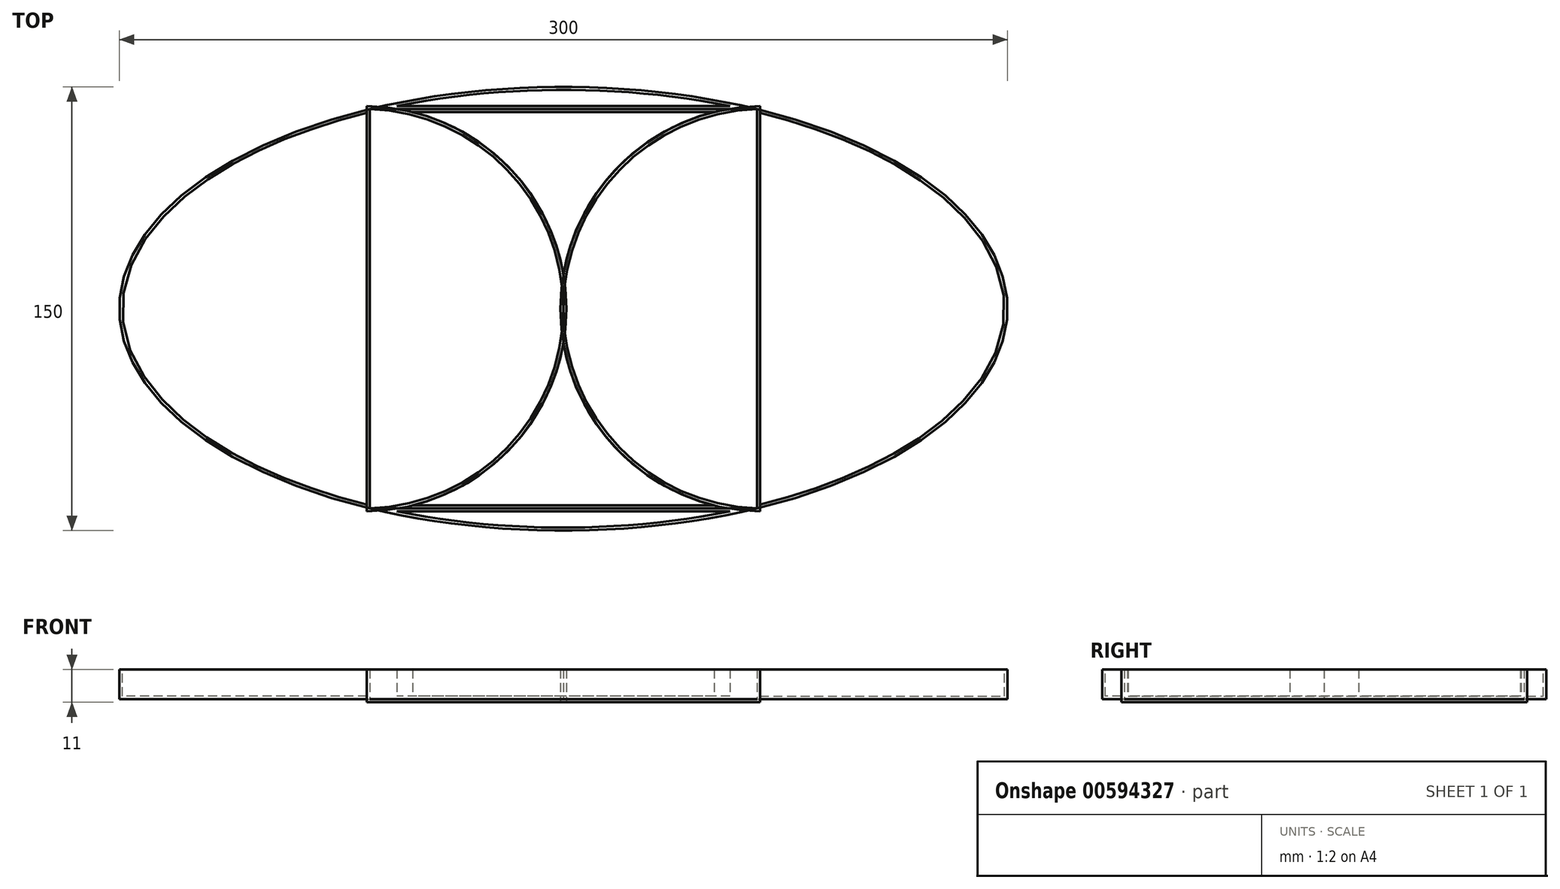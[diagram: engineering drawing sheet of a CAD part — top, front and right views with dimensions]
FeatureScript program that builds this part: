
annotation { "Feature Type Name" : "Feature", "Feature Type Description" : "" }
export const myFeature = defineFeature(function(context is Context, id is Id, definition is map)
    precondition{}
    {
        {
            var Q0;
            Q0=qCreatedBy(makeId("Top.planeOp"),FACE);
            var sketch = newSketch(context, id + "F0", { "sketchPlane" : qUnion([Q0])});
            skEllipse(sketch, "E0", {"center": v(0, 0) * mm, "majorRadius": 150 * mm, "minorRadius": 75 * mm, "majorAxis": v(1, 0)});
            skLineSegment(sketch, "E1.bottom", {"start": v(65.38, 67.5) * mm, "end": v(-65.38, 67.5) * mm});
            skLineSegment(sketch, "E1.top", {"start": v(65.38, -67.5) * mm, "end": v(-65.38, -67.5) * mm});
            skLineSegment(sketch, "E1.left", {"start": v(65.38, 67.5) * mm, "end": v(65.38, -67.5) * mm});
            skLineSegment(sketch, "E1.right", {"start": v(-65.38, 67.5) * mm, "end": v(-65.38, -67.5) * mm});
            skArc(sketch, "E2", {"start": v(-65.38, -67.5) * mm, "mid": v(0, 0) * mm, "end": v(-65.38, 67.5) * mm});
            skArc(sketch, "E3", {"start": v(65.38, 67.5) * mm, "mid": v(0, 0) * mm, "end": v(65.38, -67.5) * mm});
            skSolve(sketch);
        }
        {
            var Q0;
            {var subQ1=sQuery(id+"F0.wireOp",EDGE,"E1.right");Q0=makeQuery(id+"F0.imprint","IMPRINT",FACE,{"disambiguationData":[TD([[makeQuery(id+"F0.imprint","IMPRINT",EDGE,{"derivedFrom":subQ1}),-1.0]])]});}
            var Q1;
            {var subQ0=sQuery(id+"F0.wireOp",EDGE,"E1.bottom");Q1=makeQuery(id+"F0.imprint","IMPRINT",FACE,{"disambiguationData":[TD([[makeQuery(id+"F0.imprint","IMPRINT",EDGE,{"derivedFrom":subQ0}),-1.0]])]});}
            var Q2;
            {var subQ1=sQuery(id+"F0.wireOp",EDGE,"E1.left");Q2=makeQuery(id+"F0.imprint","IMPRINT",FACE,{"disambiguationData":[TD([[makeQuery(id+"F0.imprint","IMPRINT",EDGE,{"derivedFrom":subQ1}),1.0]])]});}
            var Q3;
            {var subQ0=sQuery(id+"F0.wireOp",EDGE,"E1.top");Q3=makeQuery(id+"F0.imprint","IMPRINT",FACE,{"disambiguationData":[TD([[makeQuery(id+"F0.imprint","IMPRINT",EDGE,{"derivedFrom":subQ0}),1.0]])]});}
            extrude(context, id + "F1", {"entities" : qUnion([Q0, Q1, Q2, Q3]), "depth" : 10 * mm, "offsetDistance" : 25 * mm});
        }
        {
            var Q0;
            Q0=makeQuery(id+"F1.opExtrude","CAP_FACE",FACE,{"disambiguationData":[OSD([sQuery(id+"F0.wireOp",EDGE,"E0"),sQuery(id+"F0.wireOp",EDGE,"E1.right")])],"isStart":false});
            var Q1;
            Q1=makeQuery(id+"F1.opExtrude","CAP_FACE",FACE,{"disambiguationData":[OSD([sQuery(id+"F0.wireOp",EDGE,"E0"),sQuery(id+"F0.wireOp",EDGE,"E1.bottom")])],"isStart":false});
            var Q2;
            Q2=makeQuery(id+"F1.opExtrude","CAP_FACE",FACE,{"disambiguationData":[OSD([sQuery(id+"F0.wireOp",EDGE,"E0"),sQuery(id+"F0.wireOp",EDGE,"E1.left")])],"isStart":false});
            var Q3;
            Q3=makeQuery(id+"F1.opExtrude","CAP_FACE",FACE,{"disambiguationData":[OSD([sQuery(id+"F0.wireOp",EDGE,"E0"),sQuery(id+"F0.wireOp",EDGE,"E1.top")])],"isStart":false});
            shell(context, id + "F2", {"entities" : qUnion([Q0, Q1, Q2, Q3]), "thickness" : 1 * mm});
        }
        {
            var Q0;
            {var subQ0=sQuery(id+"F0.wireOp",EDGE,"E1.bottom");Q0=makeQuery(id+"F0.imprint","IMPRINT",FACE,{"disambiguationData":[TD([[makeQuery(id+"F0.imprint","IMPRINT",EDGE,{"derivedFrom":subQ0}),1.0]])]});}
            var Q1;
            {var subQ0=sQuery(id+"F0.wireOp",EDGE,"E1.top");Q1=makeQuery(id+"F0.imprint","IMPRINT",FACE,{"disambiguationData":[TD([[makeQuery(id+"F0.imprint","IMPRINT",EDGE,{"derivedFrom":subQ0}),-1.0]])]});}
            extrude(context, id + "F3", {"entities" : qUnion([Q0, Q1]), "depth" : 10 * mm, "offsetDistance" : 25 * mm});
        }
        {
            var Q0;
            Q0=makeQuery(id+"F3.opExtrude","CAP_FACE",FACE,{"disambiguationData":[OSD([sQuery(id+"F0.wireOp",EDGE,"E1.bottom"),sQuery(id+"F0.wireOp",EDGE,"E2"),sQuery(id+"F0.wireOp",EDGE,"E3")])],"isStart":false});
            var Q1;
            Q1=makeQuery(id+"F3.opExtrude","CAP_FACE",FACE,{"disambiguationData":[OSD([sQuery(id+"F0.wireOp",EDGE,"E1.top"),sQuery(id+"F0.wireOp",EDGE,"E2"),sQuery(id+"F0.wireOp",EDGE,"E3")])],"isStart":false});
            shell(context, id + "F4", {"entities" : qUnion([Q0, Q1]), "thickness" : 1 * mm});
        }
        {
            var Q0;
            {var subQ0=sQuery(id+"F0.wireOp",EDGE,"E1.right");Q0=makeQuery(id+"F0.imprint","IMPRINT",FACE,{"disambiguationData":[TD([[makeQuery(id+"F0.imprint","IMPRINT",EDGE,{"derivedFrom":subQ0}),1.0]])]});}
            var Q1;
            {var subQ0=sQuery(id+"F0.wireOp",EDGE,"E1.left");Q1=makeQuery(id+"F0.imprint","IMPRINT",FACE,{"disambiguationData":[TD([[makeQuery(id+"F0.imprint","IMPRINT",EDGE,{"derivedFrom":subQ0}),-1.0]])]});}
            extrude(context, id + "F5", {"entities" : qUnion([Q0, Q1]), "depth" : 10 * mm, "offsetDistance" : 25 * mm});
        }
        {
            var Q0;
            Q0=makeQuery(id+"F5.opExtrude","CAP_FACE",FACE,{"disambiguationData":[OSD([sQuery(id+"F0.wireOp",EDGE,"E1.right"),sQuery(id+"F0.wireOp",EDGE,"E2")])],"isStart":false});
            var Q1;
            Q1=makeQuery(id+"F5.opExtrude","CAP_FACE",FACE,{"disambiguationData":[OSD([sQuery(id+"F0.wireOp",EDGE,"E1.left"),sQuery(id+"F0.wireOp",EDGE,"E3")])],"isStart":false});
            shell(context, id + "F6", {"entities" : qUnion([Q0, Q1]), "thickness" : 1 * mm, "oppositeDirection" : true});
        }
    });
